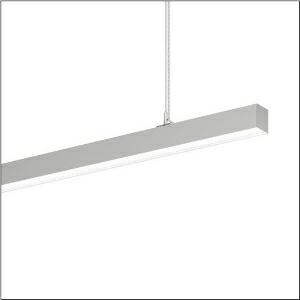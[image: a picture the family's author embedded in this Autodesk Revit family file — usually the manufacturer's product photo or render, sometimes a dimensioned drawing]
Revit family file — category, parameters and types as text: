
# Revit family: silica_r__21_51mx33da47sb_3209
name_source: partatom
category: Lighting Fixtures
units: mm (PartAtom-declared; Revit-internal decimal feet)

## family parameters
Cut with Voids When Loaded = No
Host = Face
Light Source = No
Part Type = Normal
Room Calculation Point = No
Round Connector Dimension = Use Diameter
Shared = No

## types (1)
- --- (1 x LED, 5910 lm, 38.4 W, 4000K)
    Apparent Load = 38 VA
    CIE Flux Codes = 78 96 99 55 100
    Color Rendering = 80
    Color Temperature = 4000K
    Default Elevation = 1800 mm
    Description = Silica® 21, office luminaire, primary optical cover: prismatic diffuser, of PMMA, CAT 2 (L<= 3000cd/m²), light emission: direct/indirect distribution, primary light characteristic: symmetric, installation type: suspended mounting, LED, rated luminous flux: 5.910lm, luminous efficacy: 154lm/W, light colour: 840, colour temperature: 4000K, control gear: DALI 2, with terminal, 3+2-pole, max. 2.5mm², mains connection: 220..240V, AC, 50/60Hz, rated input power: 38.4W, luminaire housing, of aluminium, metallic grey (RAL 9006), length: 1.204mm, width: 53mm, height: 53mm, protection rating (complete): IP20, insulation class (complete): insulation class I (protective earthing), certification: CE, permissible operating ambient temperature: 0..+35°C, standard: EN 50419, packaging unit: 1 piece
    Height = 53 mm
    Lamp = 1 x LED
    Lamp Light Flux = 5910 lm
    Lamp Power = 38.4 W
    Lamp count = 1
    Length = 1204 mm
    Luminous efficacy = 154 lm/W
    Manufacturer = Siteco
    ModVariant = No
    Model = 51MX33DA47SB
    Mounting Place = Ceiling
    Mounting Type = Pendant
    Number of Poles = 1
    OnlyDefault = Yes
    Power Factor = 1
    Product Name = Silica® 21
    Product group = office luminaire | ceiling pendant
    ProductGroupID = 903
    Protection Class = Protection class I
    Protection Degree = IP 20
    RLX_Detail_Level = 1
    RLX_Emergency_Light_Flux = 0 lm
    RLX_Emergency_Type = 0
    RLX_Emergency_Type_DB = No
    RlxData = <blob elided: 23113 chars, md5=53ffb187>
    Socket = socket
    Standby Power = 0 W
    System Light Flux = 5910 lm
    System Power = 38 W
    Type Comments = factory setting: luminous flux: 100 % | dim-lin: 254 | 322 mA
    Type Image = l_1335864.jpg
    URL = http://relux.com
    VarID = @adj_140109
    Voltage = 0 V
    Weight = 0.00 kg
    Width = 53 mm

## geometry (parser evidence)
native form markers: Blend x4, Sweep x11
no freeform markers — native parametric forms only
